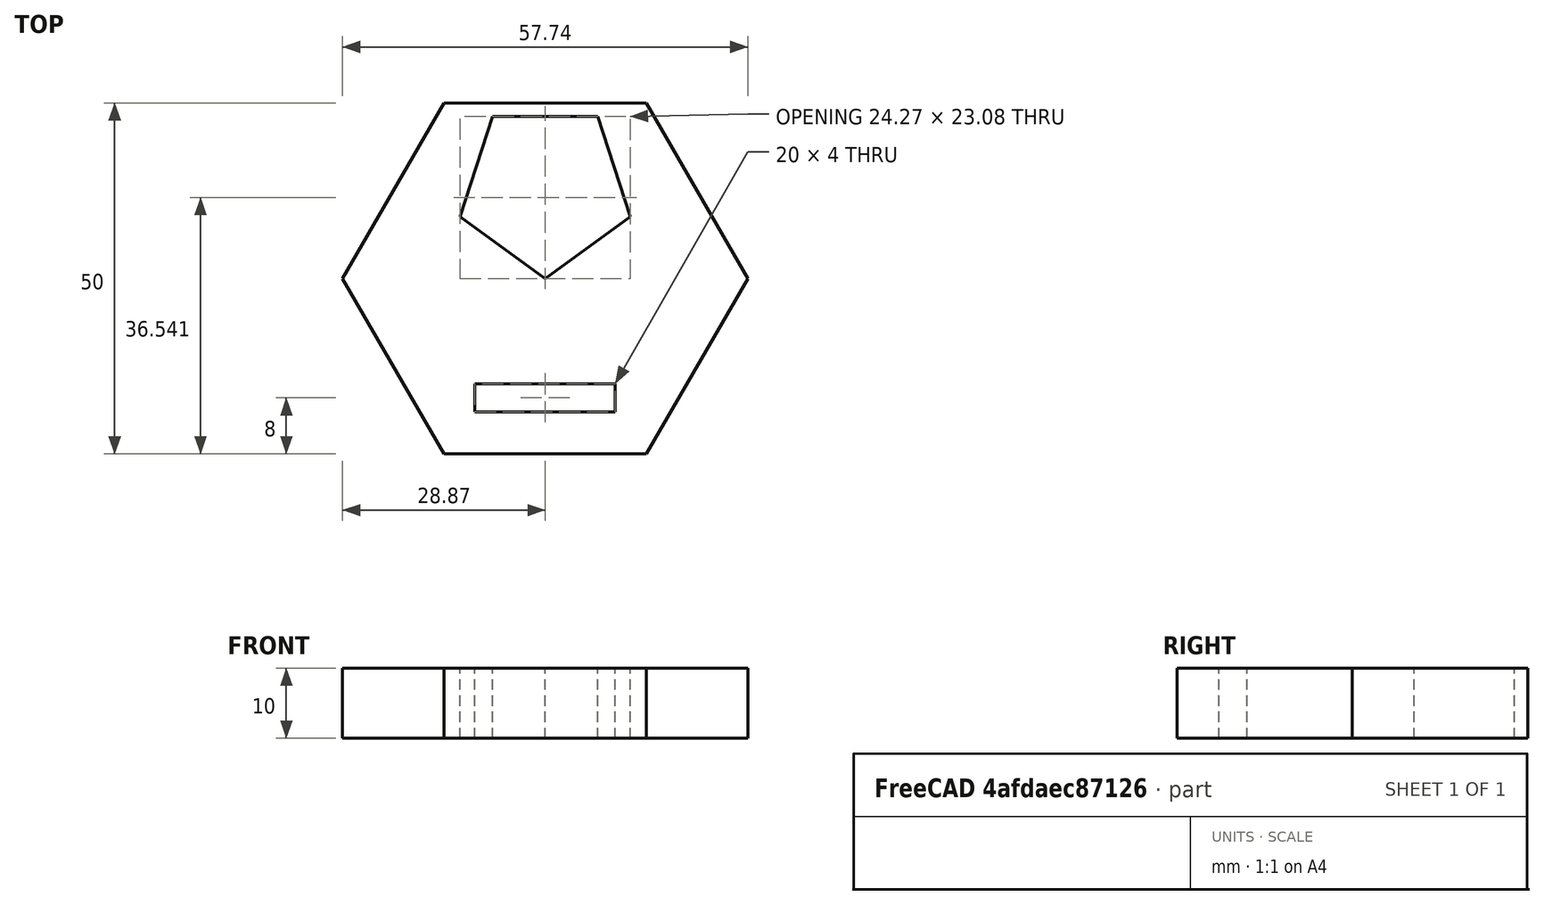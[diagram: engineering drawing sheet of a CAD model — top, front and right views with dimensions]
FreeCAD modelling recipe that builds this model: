
FCSTD DOCUMENT  (FreeCAD 1.0R39109 (Git))
Label: multi_hole_poly
License: All rights reserved
LicenseURL: https://en.wikipedia.org/wiki/All_rights_reserved
objects: Sketcher::SketchObject×1, Part::Extrusion×1
note: 3 computed .brp shape members not serialized (recipe doc carries the construction recipe); baked Part::Feature solids carry a one-line shape summary decoded from their .brp

FEATURE [Sketcher::SketchObject] Sketch
  ArcFitTolerance = 1e-06
  FullyConstrained = true
  MakeInternals = false
  sketch-geometry (17):
    g0: LineSegment StartX=28.8675 StartY=0 StartZ=0 EndX=14.4338 EndY=25 EndZ=0
    g1: LineSegment StartX=14.4338 StartY=25 StartZ=0 EndX=-14.4338 EndY=25 EndZ=0
    g2: LineSegment StartX=-14.4338 StartY=25 StartZ=0 EndX=-28.8675 EndY=-1.07e-14 EndZ=0
    g3: LineSegment StartX=-28.8675 StartY=-1.07e-14 StartZ=0 EndX=-14.4338 EndY=-25 EndZ=0
    g4: LineSegment StartX=-14.4338 StartY=-25 StartZ=0 EndX=14.4338 EndY=-25 EndZ=0
    g5: LineSegment StartX=14.4338 StartY=-25 StartZ=0 EndX=28.8675 EndY=0 EndZ=0
    g6: Circle [constr] CenterX=0 CenterY=0 CenterZ=0 NormalX=0 NormalY=0 NormalZ=1 AngleXU=0 Radius=28.8675
    g7: LineSegment StartX=7.5 StartY=23.0826 StartZ=0 EndX=-7.5 EndY=23.0826 EndZ=0
    g8: LineSegment StartX=-7.5 StartY=23.0826 StartZ=0 EndX=-12.1353 EndY=8.81678 EndZ=0
    g9: LineSegment StartX=-12.1353 StartY=8.81678 StartZ=0 EndX=0 EndY=0 EndZ=0
    g10: LineSegment StartX=0 StartY=0 StartZ=0 EndX=12.1353 EndY=8.81678 EndZ=0
    g11: LineSegment StartX=12.1353 StartY=8.81678 StartZ=0 EndX=7.5 EndY=23.0826 EndZ=0
    g12: Circle [constr] CenterX=-3.1e-15 CenterY=12.7598 CenterZ=0 NormalX=0 NormalY=0 NormalZ=1 AngleXU=0 Radius=12.7598
    g13: LineSegment StartX=-10 StartY=-15 StartZ=0 EndX=-10 EndY=-19 EndZ=0
    g14: LineSegment StartX=-10 StartY=-19 StartZ=0 EndX=10 EndY=-19 EndZ=0
    g15: LineSegment StartX=10 StartY=-19 StartZ=0 EndX=10 EndY=-15 EndZ=0
    g16: LineSegment StartX=10 StartY=-15 StartZ=0 EndX=-10 EndY=-15 EndZ=0
  constraints (42):
    c: Coincident(g0,g1)
    c: Coincident(g1,g2)
    c: Coincident(g2,g3)
    c: Coincident(g3,g4)
    c: Coincident(g4,g5)
    c: Coincident(g5,g0)
    c: Equal(g0, g1-g5) x5
    c: PointOnObject(g0,g6)
    c: PointOnObject(g1,g6)
    c: PointOnObject(g2,g6)
    c: PointOnObject(g3,g6)
    c: PointOnObject(g4,g6)
    c: PointOnObject(g5,g6)
    c: PointOnObject(g5,g-1)
    c: Distance(g5,g2) = 50
    c: Coincident(g7,g8)
    c: Coincident(g8,g9)
    c: Coincident(g9,g10)
    c: Coincident(g10,g11)
    c: Coincident(g11,g7)
    c: Equal(g7, g8-g11) x4
    c: PointOnObject(g7,g12)
    c: PointOnObject(g8,g12)
    c: PointOnObject(g9,g12)
    c: PointOnObject(g10,g12)
    c: PointOnObject(g11,g12)
    c: Distance(g9,g9) = 15
    c: Horizontal(g7)
    c: Coincident(g9,g6)
    c: Coincident(g6,g-1)
    c: Coincident(g13,g14)
    c: Coincident(g14,g15)
    c: Coincident(g15,g16)
    c: Coincident(g16,g13)
    c: Vertical(g13)
    c: Vertical(g15)
    c: Horizontal(g14)
    c: Horizontal(g16)
    c: DistanceX(g16,g16) = 20
    c: Distance(g15,g15) = 4
    c: Distance(g13,g-1) = 15
    c: Distance(g13,g-2) = 10
FEATURE [Part::Extrusion] Extrude
  Base = -> Sketch
  Dir = (0,0,1)
  DirMode = 2
  FaceMakerClass = Part::FaceMakerBullseye
  FaceMakerMode = 3
  LengthFwd = 10
  LengthRev = 0
  Solid = true
  Symmetric = false
